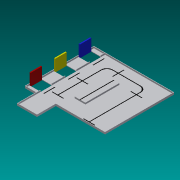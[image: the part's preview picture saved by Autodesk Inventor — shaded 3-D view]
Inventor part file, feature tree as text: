
AUTODESK INVENTOR PART (.ipt)
format: ipt  version: 2015 (Build 190159000, 159)  size: 335,872 bytes
history: native  units: mm
features: extrude x7, sketch x7, other x1
ambient origin geometry x8: Origin, YZ Plane, XZ Plane, XY Plane, X Axis, Y Axis, Z Axis, Center Point
bodies: Body1 (feature_tree)
feature tree (15):
  other  "ソリッド1"
  extrude  "押し出し1"  Depth=1800.0mm
  extrude  "押し出し2"  Depth=500.0mm
  extrude  "押し出し3"  Depth=300.0mm
  extrude  "押し出し4"  Depth=250.0mm
  extrude  "押し出し5"  Depth=650.0mm
  extrude  "押し出し6"  Depth=300.0mm
  extrude  "押し出し7"  Depth=300.0mm
  sketch  "スケッチ1"
  sketch  "スケッチ2"
  sketch  "スケッチ4"
  sketch  "スケッチ5"
  sketch  "スケッチ6"
  sketch  "スケッチ7"
  sketch  "スケッチ8"
